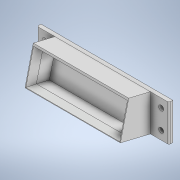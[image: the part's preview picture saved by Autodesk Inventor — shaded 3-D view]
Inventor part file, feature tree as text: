
AUTODESK INVENTOR PART (.ipt)
format: ipt  version: 2020 (Build 240168000, 168)  size: 193,536 bytes
history: native  units: in
note: dims shown in document units (in); Inventor stores cm internally (conversion verified against a paired STEP export)
features: sketch x6, extrude x4, chamfer x3, sweep x1, fillet x1
ambient origin geometry x8: Origin, YZ Plane, XZ Plane, XY Plane, X Axis, Y Axis, Z Axis, Center Point
bodies: Solid1 (feature_tree), Solid2 (feature_tree)
feature tree (15):
  extrude  "Extrusion1"  Depth=1.8543in
  sketch  "Sketch2"  dims[d2=0.1969in d3=0.0in d4=4.8425in]
  extrude  "Extrusion3"  Depth=4.8425in
  sweep  "Sweep1"
  extrude  "Extrusion4"  Depth=0.1102in
  extrude  "Extrusion5"  Depth=0.9449in
  fillet  "Fillet3"  Radius=0.2559in
  chamfer  "Chamfer11"  Distance=0.3937in
  chamfer  "Chamfer12"  Distance=0.9843in
  chamfer  "Chamfer13"  Distance=0.4331in
  sketch  "Sketch1"  dims[d0=6.6929in d1=1.8543in]
  sketch  "Sketch3"  dims[d5=4.6063in d6=0.1181in]
  sketch  "Sketch4"  dims[d7=0.1102in d8=0.1102in]
  sketch  "Sketch5"  dims[d9=0.9449in d21=0.2559in d22=0.2559in]
  sketch  "Sketch6"  dims[d23=0.3937in d24=0.3937in d25=0.9843in d26=0.4331in d27=3.3465in d28=2.3622in d29=0.0in d30=0.5257in d31=0.0in d32=0.0in d42=0.0928in d43=2.3622in d44=0.0in d47=0.0in d48=0.0in d59=0.0928in d63=0.0787in d64=0.0787in d65=0.0787in d66=0.5497in d67=0.0787in d68=0.0787in d69=0.5497in d70=0.0787in d71=0.0787in d72=0.5497in]
